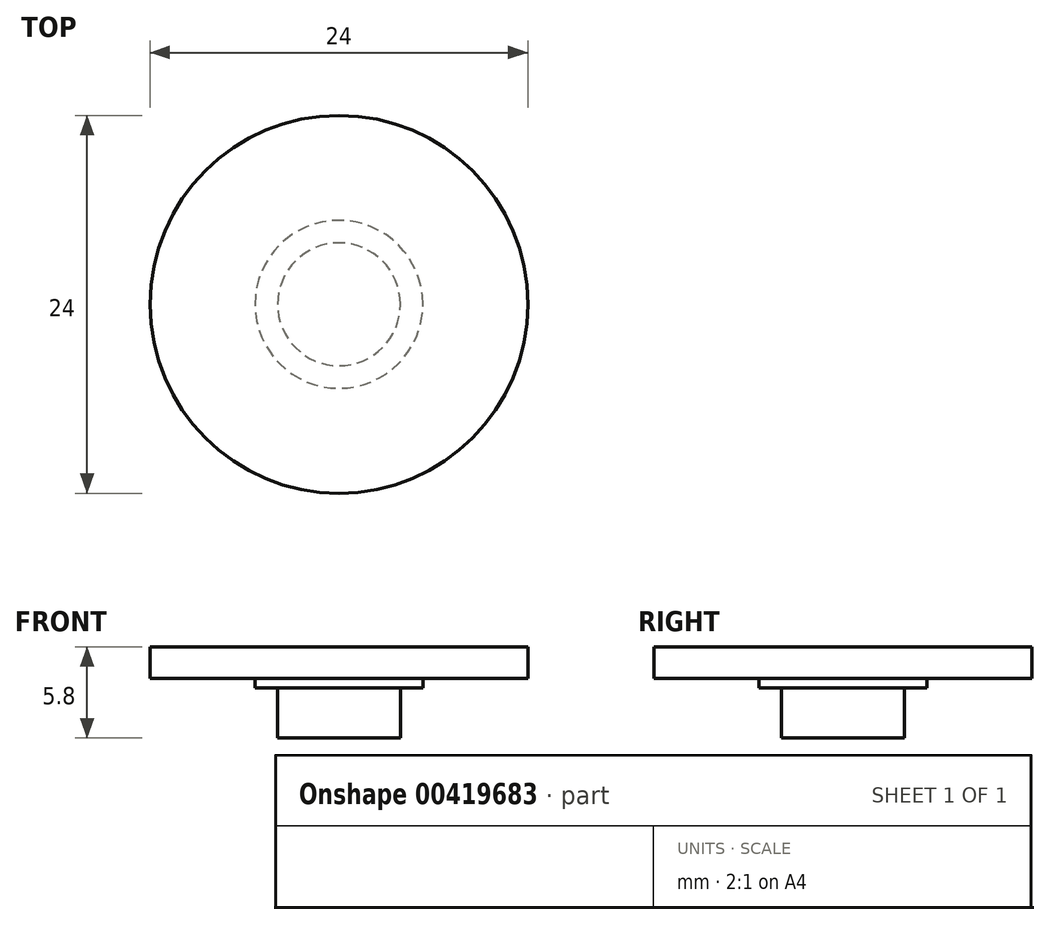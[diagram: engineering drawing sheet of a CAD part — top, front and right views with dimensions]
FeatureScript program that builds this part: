
annotation { "Feature Type Name" : "Feature", "Feature Type Description" : "" }
export const myFeature = defineFeature(function(context is Context, id is Id, definition is map)
    precondition{}
    {
        {
            var Q0;
            Q0=qCreatedBy(makeId("Front.planeOp"),FACE);
            var sketch = newSketch(context, id + "F0", { "sketchPlane" : qUnion([Q0])});
            skLineSegment(sketch, "E0", {"start": v(-3.9, 0) * mm, "end": v(-3.9, 3.2) * mm});
            skLineSegment(sketch, "E1", {"start": v(-3.9, 3.2) * mm, "end": v(-5.33, 3.2) * mm});
            skLineSegment(sketch, "E2", {"start": v(-5.33, 3.2) * mm, "end": v(-5.33, 3.8) * mm});
            skLineSegment(sketch, "E3", {"start": v(-5.33, 3.8) * mm, "end": v(-12, 3.8) * mm});
            skLineSegment(sketch, "E4", {"start": v(-12, 3.8) * mm, "end": v(-12, 5.8) * mm});
            skLineSegment(sketch, "E5", {"start": v(-12, 5.8) * mm, "end": v(0, 5.8) * mm});
            skLineSegment(sketch, "E6", {"start": v(-3.9, 0) * mm, "end": v(0, 0) * mm});
            skLineSegment(sketch, "E7", {"start": v(0, 5.8) * mm, "end": v(0, 0) * mm});
            skSolve(sketch);
        }
        {
            var Q0;
            Q0=makeQuery(id+"F0.imprint","IMPRINT",FACE,{"disambiguationData":[TD([[makeQuery(id+"F0.imprint","IMPRINT",EDGE,{"derivedFrom":sQuery(id+"F0.wireOp",EDGE,"E0")}),-1.0]])]});
            var Q1;
            Q1=sQuery(id+"F0.wireOp",EDGE,"E7");
            revolve(context, id + "F1", {"entities" : qUnion([Q0]), "axis" : qUnion([Q1]), "revolveType" : RevolveType.FULL});
        }
    });
